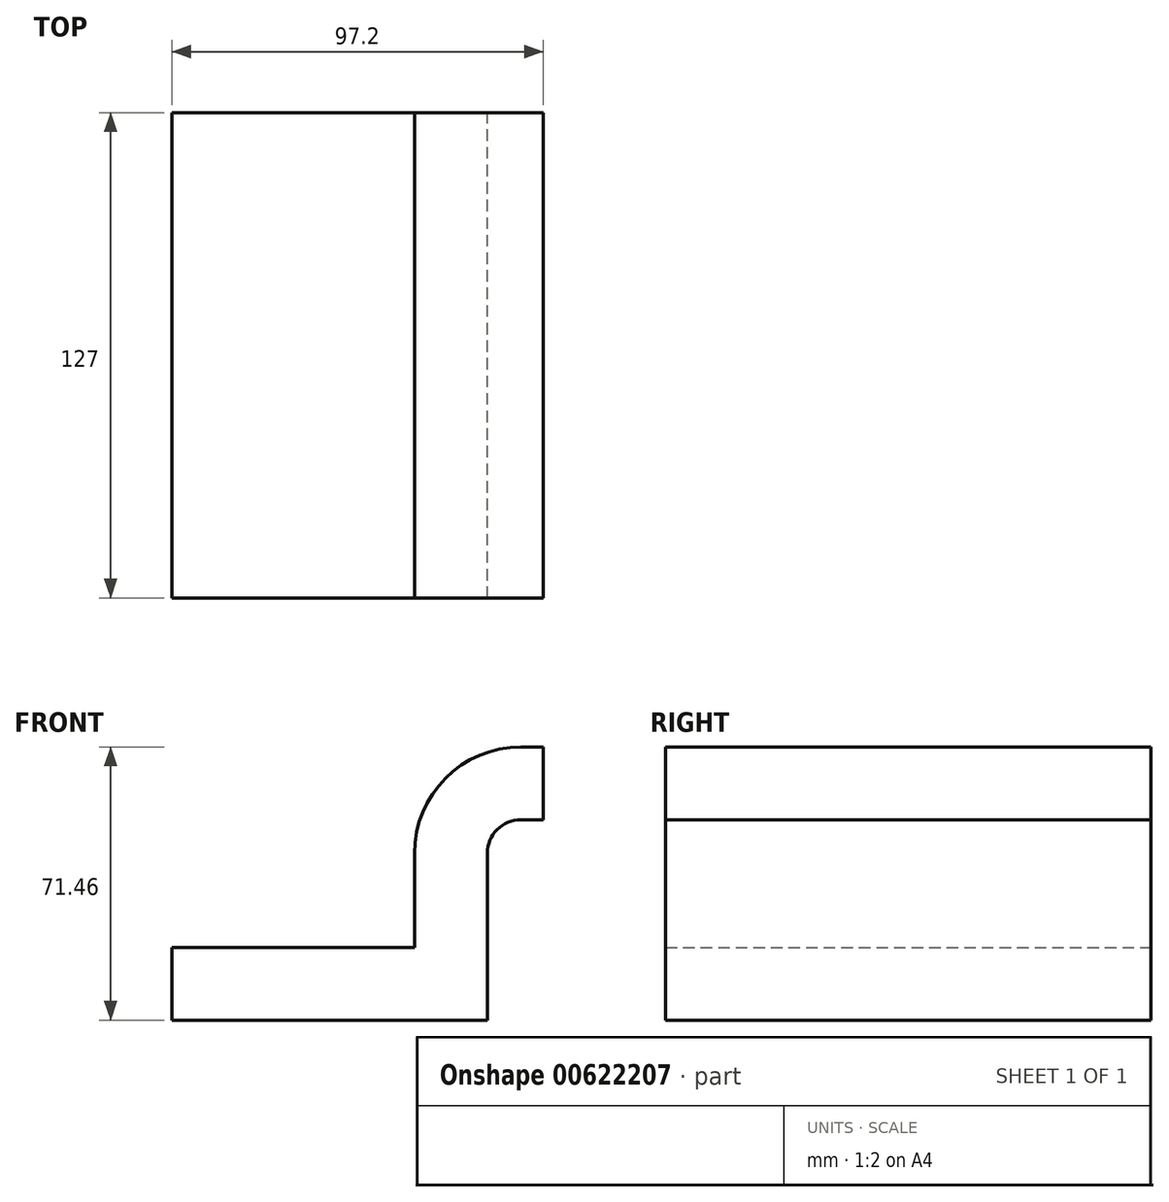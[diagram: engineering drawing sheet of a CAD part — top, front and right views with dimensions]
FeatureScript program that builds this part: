
annotation { "Feature Type Name" : "Feature", "Feature Type Description" : "" }
export const myFeature = defineFeature(function(context is Context, id is Id, definition is map)
    precondition{}
    {
        {
            var Q0;
            Q0=qCreatedBy(makeId("Front.planeOp"),FACE);
            var sketch = newSketch(context, id + "F0", { "sketchPlane" : qUnion([Q0])});
            skLineSegment(sketch, "E0.bottom", {"start": v(41.28, -9.52) * mm, "end": v(-41.28, -9.53) * mm});
            skLineSegment(sketch, "E0.top", {"start": v(41.28, 9.53) * mm, "end": v(-41.28, 9.53) * mm});
            skLineSegment(sketch, "E0.left", {"start": v(41.28, -9.52) * mm, "end": v(41.28, 9.53) * mm});
            skLineSegment(sketch, "E0.right", {"start": v(-41.28, -9.52) * mm, "end": v(-41.28, 9.53) * mm});
            skPoint(sketch, "E0.middle", {"position": v(0, 0) * mm});
            skLineSegment(sketch, "E1.bottom", {"start": v(106.73, 38.1) * mm, "end": v(55.93, 38.1) * mm});
            skLineSegment(sketch, "E1.top", {"start": v(106.73, 66.68) * mm, "end": v(55.93, 66.68) * mm});
            skLineSegment(sketch, "E1.left", {"start": v(106.73, 38.1) * mm, "end": v(106.73, 66.68) * mm});
            skLineSegment(sketch, "E1.right", {"start": v(55.93, 38.1) * mm, "end": v(55.93, 66.68) * mm});
            skPoint(sketch, "E1.middle", {"position": v(81.33, 52.39) * mm});
            skLineSegment(sketch, "E2", {"start": v(41.28, 9.53) * mm, "end": v(41.28, 34.05) * mm});
            skArc(sketch, "E3", {"start": v(41.27, 34.05) * mm, "mid": v(43.86, 40.3) * mm, "end": v(50.1, 42.88) * mm});
            skLineSegment(sketch, "E4", {"start": v(50.1, 42.88) * mm, "end": v(80.45, 42.88) * mm});
            skLineSegment(sketch, "E5.0", {"start": v(50.1, 61.93) * mm, "end": v(80.76, 61.93) * mm});
            skArc(sketch, "E5.1", {"start": v(22.22, 34.05) * mm, "mid": v(30.39, 53.76) * mm, "end": v(50.1, 61.93) * mm});
            skLineSegment(sketch, "E5.2", {"start": v(22.22, 9.53) * mm, "end": v(22.22, 34.05) * mm});
            skLineSegment(sketch, "E6", {"start": v(81.33, 52.39) * mm, "end": v(81.33, 66.68) * mm});
            skFitSpline(sketch, "E7", {"points": [v(-41.28, 9.52) * mm, v(50.1, 61.93) * mm], "startDerivative": vector(60.28, 92.73) * mm, "endDerivative": vector(136.7, -5.25) * mm});
            skSolve(sketch);
        }
        {
            var Q0;
            Q0=makeQuery(id+"F0.imprint","IMPRINT",FACE,{"disambiguationData":[TD([[makeQuery(id+"F0.imprint","IMPRINT",EDGE,{"derivedFrom":sQuery(id+"F0.wireOp",EDGE,"E0.bottom")}),-1.0]])]});
            var Q1;
            {var subQ1=sQuery(id+"F0.wireOp",EDGE,"E2");Q1=makeQuery(id+"F0.imprint","IMPRINT",FACE,{"disambiguationData":[TD([[makeQuery(id+"F0.imprint","IMPRINT",EDGE,{"derivedFrom":subQ1}),1.0]])]});}
            extrude(context, id + "F1", {"entities" : qUnion([Q0, Q1]), "endBound" : BoundingType.SYMMETRIC, "depth" : 127 * mm, "offsetDistance" : 25.4 * mm});
        }
    });
